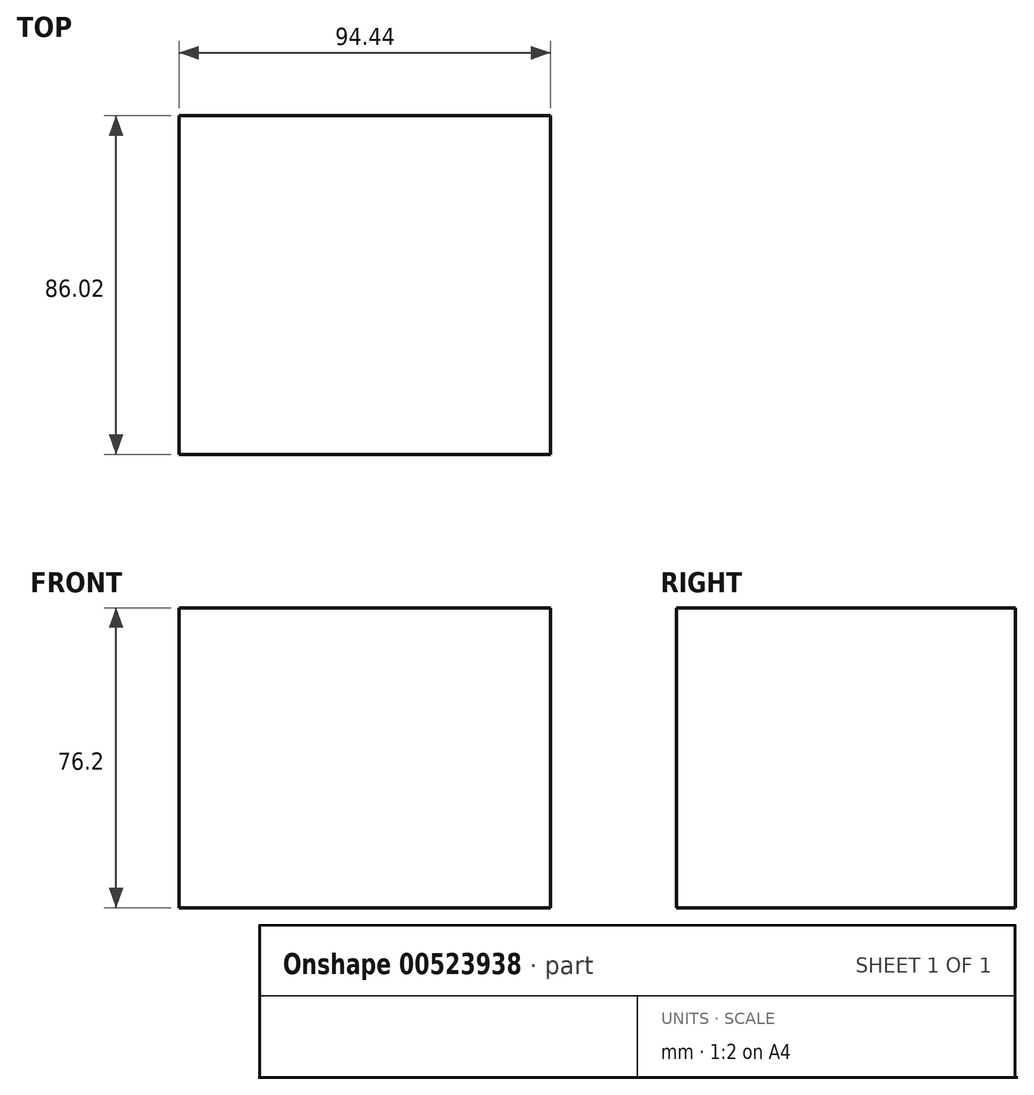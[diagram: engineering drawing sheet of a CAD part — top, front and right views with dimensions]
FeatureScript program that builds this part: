
annotation { "Feature Type Name" : "Feature", "Feature Type Description" : "" }
export const myFeature = defineFeature(function(context is Context, id is Id, definition is map)
    precondition{}
    {
        {
            var Q0;
            Q0=qCreatedBy(makeId("Top.planeOp"),FACE);
            var sketch = newSketch(context, id + "F0", { "sketchPlane" : qUnion([Q0])});
            skLineSegment(sketch, "E0.bottom", {"start": v(47.22, 43.01) * mm, "end": v(-47.22, 43.01) * mm});
            skLineSegment(sketch, "E0.top", {"start": v(47.22, -43.01) * mm, "end": v(-47.22, -43.01) * mm});
            skLineSegment(sketch, "E0.left", {"start": v(47.22, 43.01) * mm, "end": v(47.22, -43.01) * mm});
            skLineSegment(sketch, "E0.right", {"start": v(-47.22, 43.01) * mm, "end": v(-47.22, -43.01) * mm});
            skPoint(sketch, "E0.middle", {"position": v(0, 0) * mm});
            skSolve(sketch);
        }
        {
            var Q0;
            Q0 = qSketchRegion(id + "F0", true);
            extrude(context, id + "F1", {"entities" : qUnion([Q0]), "depth" : 76.2 * mm, "offsetDistance" : 25.4 * mm});
        }
    });
